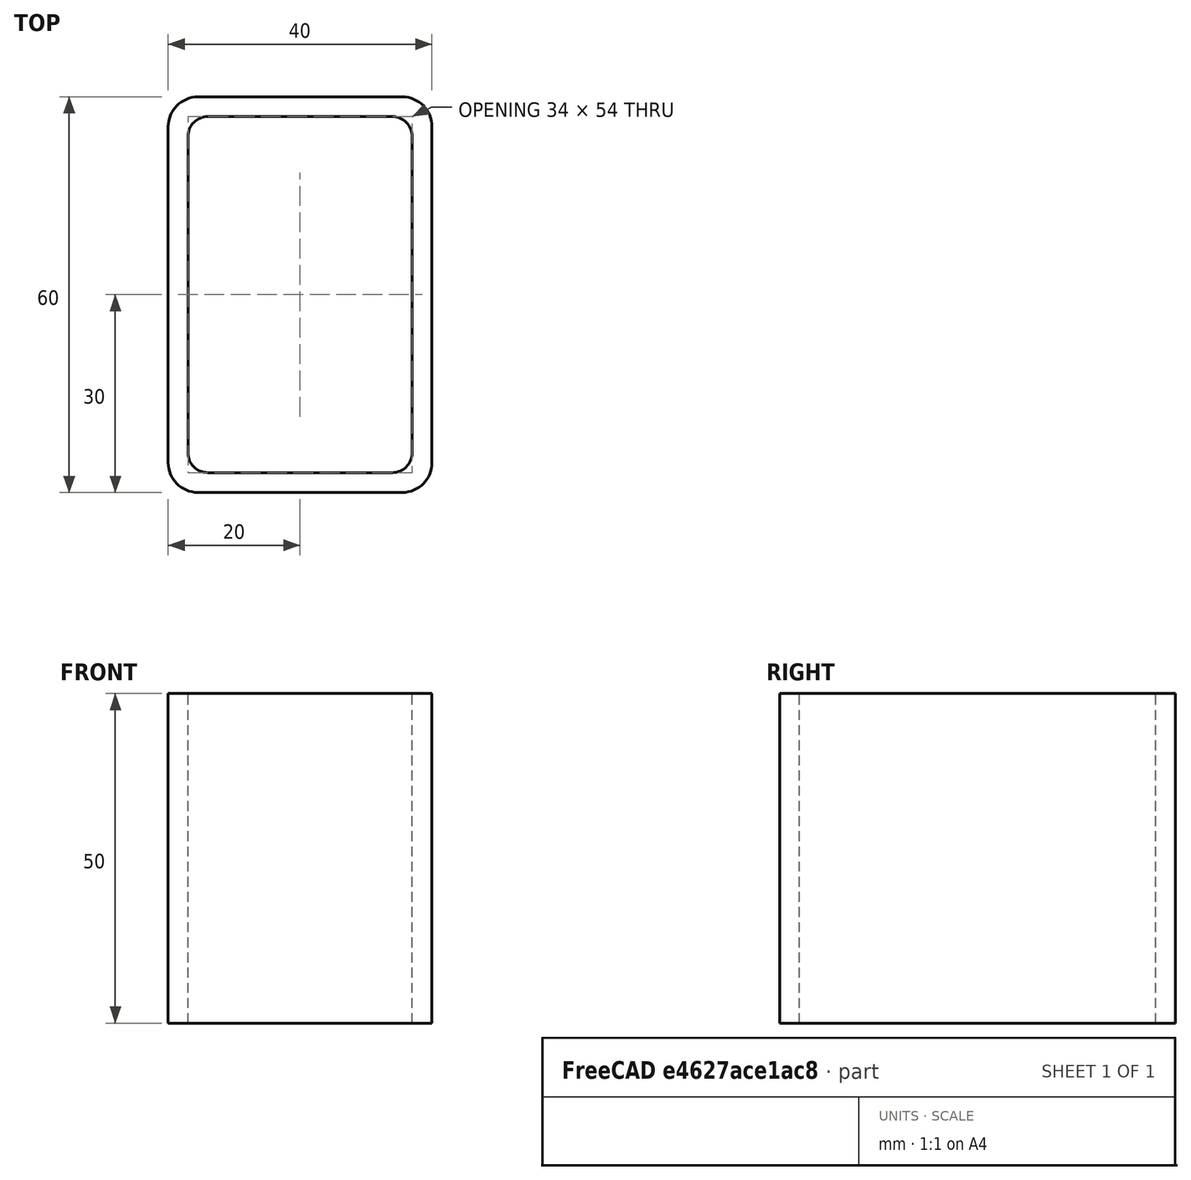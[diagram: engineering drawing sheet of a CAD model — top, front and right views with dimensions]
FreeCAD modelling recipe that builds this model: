
FCSTD DOCUMENT  (FreeCAD 0.15R4671 (Git))
Label: Rectangular hollow section 60x40x3 EN10219 S235JRH
License: All rights reserved
LicenseURL: http://en.wikipedia.org/wiki/All_rights_reserved
objects: Sketcher::SketchObject×1, Part::Extrusion×1
note: 2 computed .brp shape members not serialized (recipe doc carries the construction recipe); baked Part::Feature solids carry a one-line shape summary decoded from their .brp

FEATURE [Sketcher::SketchObject] Sketch
  sketch-geometry (16):
    g0: LineSegment StartX=-14 StartY=27 StartZ=0 EndX=14 EndY=27 EndZ=0
    g1: LineSegment StartX=17 StartY=24 StartZ=0 EndX=17 EndY=-24 EndZ=0
    g2: LineSegment StartX=14 StartY=-27 StartZ=0 EndX=-14 EndY=-27 EndZ=0
    g3: LineSegment StartX=-17 StartY=-24 StartZ=0 EndX=-17 EndY=24 EndZ=0
    g4: LineSegment StartX=-15.5 StartY=30 StartZ=0 EndX=15.5 EndY=30 EndZ=0
    g5: LineSegment StartX=20 StartY=25.5 StartZ=0 EndX=20 EndY=-25.5 EndZ=0
    g6: LineSegment StartX=15.5 StartY=-30 StartZ=0 EndX=-15.5 EndY=-30 EndZ=0
    g7: LineSegment StartX=-20 StartY=-25.5 StartZ=0 EndX=-20 EndY=25.5 EndZ=0
    g8: ArcOfCircle CenterX=-14 CenterY=24 CenterZ=0 NormalX=0 NormalY=0 NormalZ=1 Radius=3 StartAngle=1.5708 EndAngle=3.14159
    g9: ArcOfCircle CenterX=14 CenterY=24 CenterZ=0 NormalX=0 NormalY=0 NormalZ=1 Radius=3 StartAngle=0 EndAngle=1.5708
    g10: ArcOfCircle CenterX=14 CenterY=-24 CenterZ=0 NormalX=0 NormalY=0 NormalZ=1 Radius=3 StartAngle=4.71239 EndAngle=6.28319
    g11: ArcOfCircle CenterX=-14 CenterY=-24 CenterZ=0 NormalX=0 NormalY=0 NormalZ=1 Radius=3 StartAngle=3.14159 EndAngle=4.71239
    g12: ArcOfCircle CenterX=15.5 CenterY=25.5 CenterZ=0 NormalX=0 NormalY=0 NormalZ=1 Radius=4.5 StartAngle=0 EndAngle=1.5708
    g13: ArcOfCircle CenterX=15.5 CenterY=-25.5 CenterZ=0 NormalX=0 NormalY=0 NormalZ=1 Radius=4.5 StartAngle=4.71239 EndAngle=6.28319
    g14: ArcOfCircle CenterX=-15.5 CenterY=-25.5 CenterZ=0 NormalX=0 NormalY=0 NormalZ=1 Radius=4.5 StartAngle=3.14159 EndAngle=4.71239
    g15: ArcOfCircle CenterX=-15.5 CenterY=25.5 CenterZ=0 NormalX=0 NormalY=0 NormalZ=1 Radius=4.5 StartAngle=1.5708 EndAngle=3.14159
  constraints (36):
    c: Horizontal(g2)
    c: Vertical(g3)
    c: Horizontal(g6)
    c: Vertical(g7)
    c: Tangent(g3,g8) = 1.5708
    c: Tangent(g0,g8) = 1.5708
    c: Tangent(g0,g9) = 1.5708
    c: Tangent(g1,g9) = 1.5708
    c: Tangent(g1,g10) = 1.5708
    c: Tangent(g2,g10) = 1.5708
    c: Tangent(g2,g11) = 1.5708
    c: Tangent(g3,g11) = 1.5708
    c: Tangent(g4,g12) = 1.5708
    c: Tangent(g5,g12) = 1.5708
    c: Tangent(g5,g13) = 1.5708
    c: Tangent(g6,g13) = 1.5708
    c: Tangent(g6,g14) = 1.5708
    c: Tangent(g7,g14) = 1.5708
    c: Tangent(g7,g15) = 1.5708
    c: Tangent(g4,g15) = 1.5708
    c: Equal(g9,g8)
    c: Equal(g9,g11)
    c: Equal(g9,g10)
    c: Equal(g12,g15)
    c: Equal(g12,g14)
    c: Equal(g12,g13)
    c: Symmetric(g4,g6,g-1)
    c: Symmetric(g7,g5,g-2)
    c: DistanceY(g4,g6) = -60
    c: DistanceX(g7,g5) = 40
    c: Symmetric(g3,g1,g-2)
    c: Symmetric(g0,g2,g-1)
    c: DistanceY(g0,g4) = 3
    c: DistanceX(g5,g1) = -3
    c: Radius(g9) = 3
    c: Radius(g12) = 4.5
FEATURE [Part::Extrusion] Extrude  label="Rectangular hollow section 60x40x3 EN10219 S235JRH"
  Base = -> Sketch
  Dir = (0,0,50)
  Solid = true
